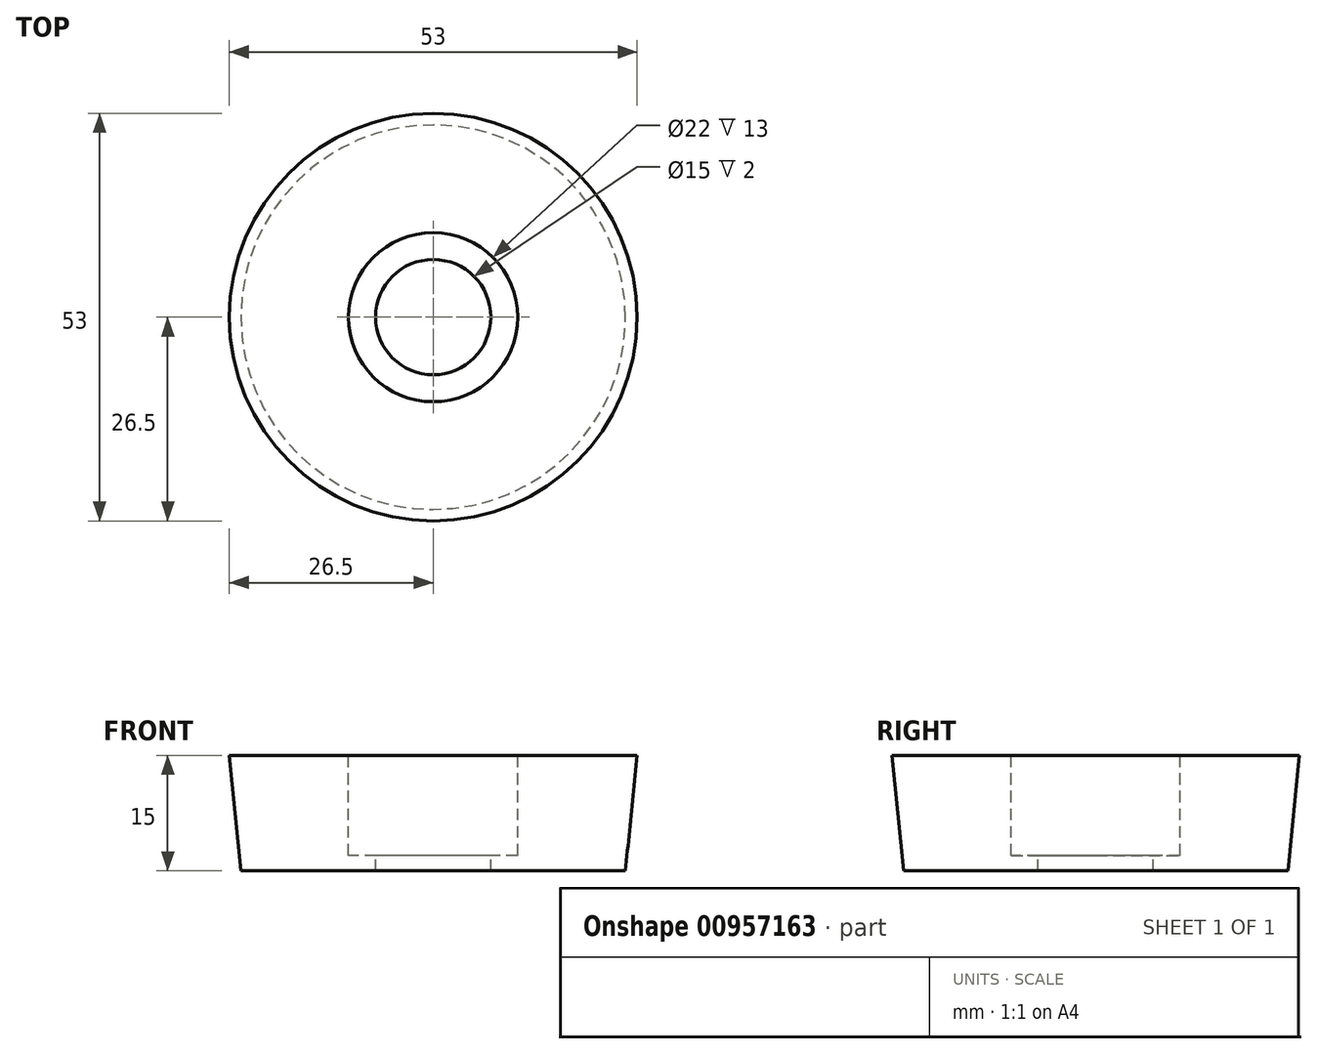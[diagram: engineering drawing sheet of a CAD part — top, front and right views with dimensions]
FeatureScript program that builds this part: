
annotation { "Feature Type Name" : "Feature", "Feature Type Description" : "" }
export const myFeature = defineFeature(function(context is Context, id is Id, definition is map)
    precondition{}
    {
        {
            var Q0;
            Q0=qCreatedBy(makeId("Top.planeOp"),FACE);
            var sketch = newSketch(context, id + "F0", { "sketchPlane" : qUnion([Q0])});
            skCircle(sketch, "E0", {"center": v(0, 0) * mm, "radius": 25 * mm});
            skSolve(sketch);
        }
        {
            var Q0;
            Q0=qCreatedBy(makeId("Top.planeOp"),FACE);
            cPlane(context, id + "F1", {"entities" : qUnion([Q0]), "cplaneType" : CPlaneType.OFFSET, "offset" : 15 * mm, "width" : 150 * mm, "height" : 150 * mm});
        }
        {
            var Q0;
            Q0=qCreatedBy(id+"F1.planeOp",FACE);
            var sketch = newSketch(context, id + "F2", { "sketchPlane" : qUnion([Q0])});
            skCircle(sketch, "E1", {"center": v(0, 0) * mm, "radius": 26.5 * mm});
            skSolve(sketch);
        }
        {
            var Q0;
            Q0=makeQuery(id+"F0.imprint","IMPRINT",FACE,{"disambiguationData":[TD([[makeQuery(id+"F0.imprint","IMPRINT",EDGE,{"derivedFrom":sQuery(id+"F0.wireOp",EDGE,"E0")}),1.0]])]});
            var Q1;
            Q1=makeQuery(id+"F2.imprint","IMPRINT",FACE,{"disambiguationData":[TD([[makeQuery(id+"F2.imprint","IMPRINT",EDGE,{"derivedFrom":sQuery(id+"F2.wireOp",EDGE,"E1")}),1.0]])]});
            loft(context, id + "F3", {"sheetProfilesArray" : [{ "sheetProfileEntities" : qUnion([Q0]) }, { "sheetProfileEntities" : qUnion([Q1]) }]});
        }
        {
            var Q0;
            Q0=makeQuery(id+"F3.opLoft","CAP_FACE",FACE,{"disambiguationData":[OSD([makeQuery(id+"F2.imprint","IMPRINT",FACE,{"disambiguationData":[TD([[makeQuery(id+"F2.imprint","IMPRINT",EDGE,{"derivedFrom":sQuery(id+"F2.wireOp",EDGE,"E1")}),1.0]])]})])],"isStart":true});
            var sketch = newSketch(context, id + "F4", { "sketchPlane" : qUnion([Q0])});
            skCircle(sketch, "E2", {"center": v(0, 0) * mm, "radius": 11 * mm});
            skSolve(sketch);
        }
        {
            var Q0;
            Q0 = qSketchRegion(id + "F4", true);
            extrude(context, id + "F5", {"entities" : qUnion([Q0]), "operationType" : NewBodyOperationType.REMOVE, "oppositeDirection" : true, "depth" : 13 * mm, "offsetDistance" : 25 * mm});
        }
        {
            var Q0;
            Q0=makeQuery(id+"F5.boolean.opBoolean","COPY",FACE,{"derivedFrom":makeQuery(id+"F5.opExtrude","CAP_FACE",FACE,{"disambiguationData":[OSD([sQuery(id+"F4.wireOp",EDGE,"E2")])],"isStart":false})});
            var sketch = newSketch(context, id + "F6", { "sketchPlane" : qUnion([Q0])});
            skCircle(sketch, "E3", {"center": v(0, 0) * mm, "radius": 7.5 * mm});
            skSolve(sketch);
        }
        {
            var Q0;
            Q0 = qSketchRegion(id + "F6", true);
            extrude(context, id + "F7", {"entities" : qUnion([Q0]), "operationType" : NewBodyOperationType.REMOVE, "oppositeDirection" : true, "depth" : 25 * mm, "offsetDistance" : 25 * mm});
        }
    });
